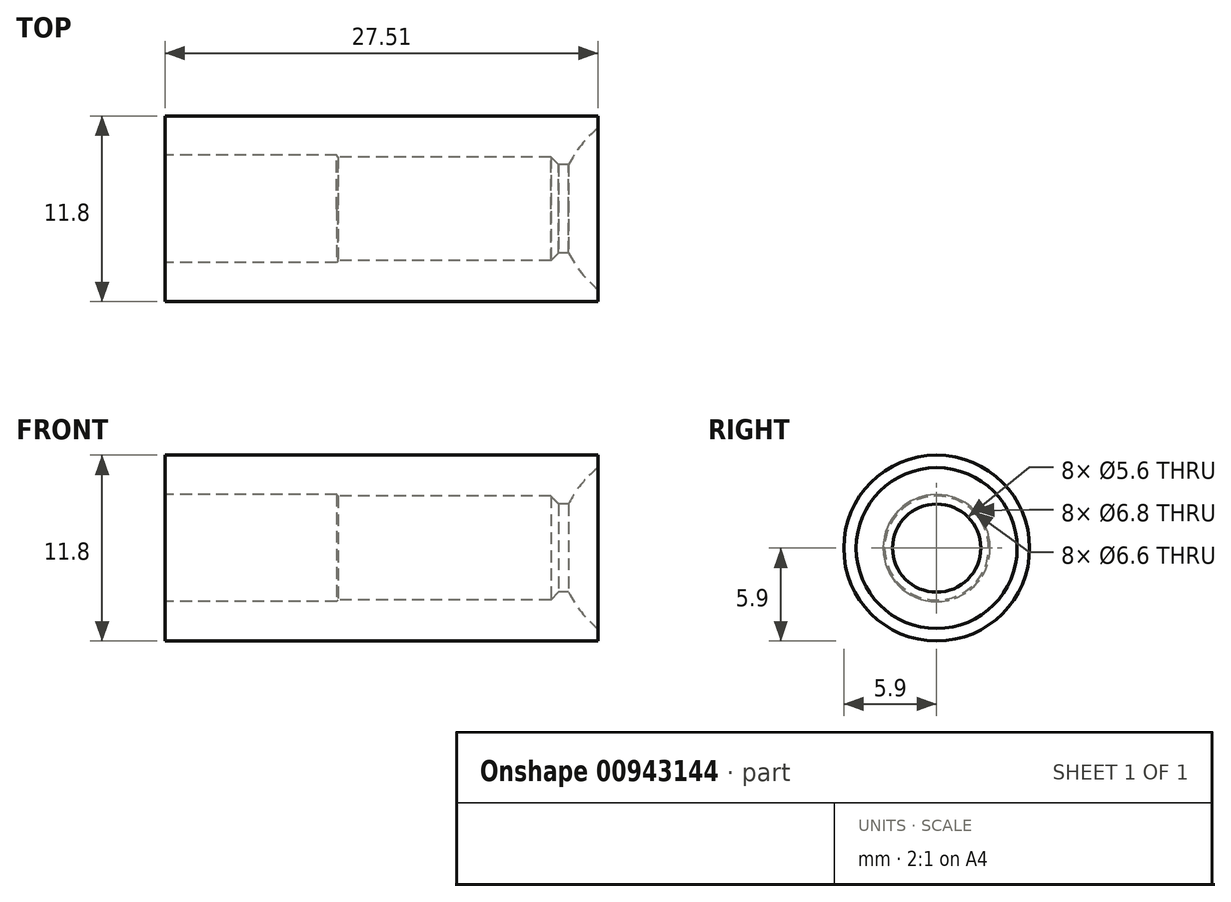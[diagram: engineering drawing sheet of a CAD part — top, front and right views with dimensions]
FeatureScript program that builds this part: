
annotation { "Feature Type Name" : "Feature", "Feature Type Description" : "" }
export const myFeature = defineFeature(function(context is Context, id is Id, definition is map)
    precondition{}
    {
        {
            var Q0;
            Q0=qCreatedBy(makeId("Top.planeOp"),FACE);
            var sketch = newSketch(context, id + "F0", { "sketchPlane" : qUnion([Q0])});
            skCircle(sketch, "E0", {"center": v(13.4, 0) * mm, "radius": 6.48 * mm});
            skLineSegment(sketch, "E1.bottom", {"start": v(-6.42, 3.3) * mm, "end": v(6.43, 3.3) * mm});
            skLineSegment(sketch, "E1.top", {"start": v(-6.42, -3.3) * mm, "end": v(6.42, -3.3) * mm});
            skLineSegment(sketch, "E1.left", {"start": v(-6.42, 3.3) * mm, "end": v(-6.42, -3.3) * mm});
            skLineSegment(sketch, "E1.right", {"start": v(6.43, 3.3) * mm, "end": v(6.43, -3.3) * mm});
            skPoint(sketch, "E1.middle", {"position": v(0, 0) * mm});
            skLineSegment(sketch, "E2.bottom", {"start": v(-7.07, 3.4) * mm, "end": v(-18.07, 3.4) * mm});
            skLineSegment(sketch, "E2.top", {"start": v(-7.07, -3.4) * mm, "end": v(-18.07, -3.4) * mm});
            skLineSegment(sketch, "E2.left", {"start": v(-7.07, 3.4) * mm, "end": v(-7.07, -3.4) * mm});
            skLineSegment(sketch, "E2.right", {"start": v(-18.07, 3.4) * mm, "end": v(-18.07, -3.4) * mm});
            skPoint(sketch, "E2.middle", {"position": v(-12.57, 0) * mm});
            skLineSegment(sketch, "E3", {"start": v(0, 0) * mm, "end": v(2.7, 0) * mm, "construction": true});
            skLineSegment(sketch, "E4", {"start": v(6.43, 1.5) * mm, "end": v(7.1, 1.5) * mm});
            skLineSegment(sketch, "E5", {"start": v(-18.07, 3.4) * mm, "end": v(-18.07, 5.9) * mm});
            skLineSegment(sketch, "E6", {"start": v(-18.07, 5.9) * mm, "end": v(10.73, 5.9) * mm});
            skLineSegment(sketch, "E7", {"start": v(-6.42, 3.3) * mm, "end": v(-7.07, 3.3) * mm});
            skLineSegment(sketch, "E8", {"start": v(9.43, 5.9) * mm, "end": v(9.43, 5.11) * mm});
            skLineSegment(sketch, "E9", {"start": v(6.93, 3.3) * mm, "end": v(6.93, 0) * mm});
            skLineSegment(sketch, "E10", {"start": v(6.93, 3.3) * mm, "end": v(6.43, 3.3) * mm});
            skLineSegment(sketch, "E11", {"start": v(6.43, 3.3) * mm, "end": v(6.93, 2.8) * mm});
            skLineSegment(sketch, "E12", {"start": v(6.93, 2.8) * mm, "end": v(7.56, 2.8) * mm});
            skSolve(sketch);
        }
        {
            var Q0;
            {var subQ0=sQuery(id+"F0.wireOp",EDGE,"E10");Q0=makeQuery(id+"F0.imprint","IMPRINT",FACE,{"disambiguationData":[TD([[makeQuery(id+"F0.imprint","IMPRINT",EDGE,{"derivedFrom":subQ0}),1.0]])]});}
            var Q1;
            Q1=makeQuery(id+"F0.imprint","IMPRINT",FACE,{"disambiguationData":[TD([[makeQuery(id+"F0.imprint","IMPRINT",EDGE,{"derivedFrom":sQuery(id+"F0.wireOp",EDGE,"E1.bottom")}),1.0]])]});
            var Q2;
            Q2=sQuery(id+"F0.wireOp",EDGE,"E3");
            revolve(context, id + "F1", {"surfaceOperationType" : NewSurfaceOperationType.NEW, "entities" : qUnion([Q0, Q1]), "axis" : qUnion([Q2]), "revolveType" : RevolveType.FULL});
        }
        {
            var Q0;
            Q0=makeQuery(id+"F1.opRevolve","SWEPT_EDGE",EDGE,{"disambiguationData":[OSD([sQuery(id+"F0.wireOp",EDGE,"E2.bottom"),sQuery(id+"F0.wireOp",EDGE,"E2.left")])]});
            chamfer(context, id + "F2", {"entities" : qUnion([Q0]), "width" : 0.1 * mm, "tangentPropagation" : true});
        }
    });
